# Revit family: LAMP_LUP DOWNLIGHT 110
name_source: partatom
category: Luminarias
revit_build: Autodesk Revit 2018 (Build: 20190510_1515(x64)
units: mm (PartAtom-declared; Revit-internal decimal feet)

## family parameters
Anfitrión = Cara
Compartido = No
Corte con vacíos al cargar = No
Cota de conector redondo = Diámetro de uso
Origen de luz = Sí
Punto de cálculo de habitación = No
Tipo de pieza = Normal

## types (8) — shared parameters
CRI = 80
Cambio de temperatura de color de luz atenuada = <Ninguno>
Diameter = 110 mm  [stored 0.360892 ft]
Elevación por defecto = 1219 mm
Filtro de color = 16777215
Finish = Texturised black RAL 9011
Gear = Electronic
Height = 155 mm  [stored 0.50853 ft]
Installation instructions = https://www.lamp.es
Insulation class = I
LED Lifetime = 50.000 L80 B10
Lamp = COB LED
Last update = 15/02/2022
MacAdam = 3
Manufacturer URL = http://www.lamp.es
Manufacturer country = Spain
Manufacturer name = LAMP
Material COB = LAMP_COB
Material cristal = LAMP_Cristal Bazz Transparente
Material cuerpo = LAMP_Aluminio Ocult Pendular NG
Material reflector = LAMP_Aluminio Reflector Imag
Product URL = https://www.lamp.es
Product datasheet = http://www.lamp.es
Protection rating = IP65 / IK06
Type = COB PHILIPS
Weight = 1.23 kg

## per-type parameters (varying)
| type | Archivo de red fotométrica | Efficacy | Plum | Power | Power Supply | Product code | Ángulo de inclinación |
| 600LM 3000 FLOOD BLACK | LS111005FL30NB.IES | 95 lm/W | 6 W | 5 W | 220-240V 50/60Hz | LS111005FL30NB | -90.00° |
| 624LM 3000 WIDE FLOOD BLACK | LS111005WF30NB.IES | 99 lm/W | 6 W | 5 W | 220-240V 50/60Hz | LS111005WF30NB | -90.00° |
| 626LM 4000 FLOOD BLACK | LS111005FL40NB.IES | 99 lm/W | 6 W | 5 W | 220-240V 50/60Hz | LS111005FL40NB | -90.00° |
| 650LM 4000 WIDE FLOOD BLACK | LS111005WF40NB.IES | 103 lm/W | 6 W | 5 W | 220-240V 50/60Hz | LS111005WF40NB | -90.00° |
| 963LM 3000 FLOOD BLACK | LS111010FL30NB.IES | 99 lm/W | 10 W | 8 W | 100-277V 50/60Hz | LS111010FL30NB | -90.00° |
| 1003LM 4000 FLOOD BLACK | LS111010FL40NB.IES | 103 lm/W | 10 W | 8 W | 100-277V 50/60Hz | LS111010FL40NB | 90.00° |
| 1008LM 3000 WIDE FLOOD BLACK | LS111010WF30NB.IES | 104 lm/W | 10 W | 8 W | 100-277V 50/60Hz | LS111010WF30NB | -90.00° |
| 1050LM 4000 WIDE FLOOD BLACK | LS111010WF40NB.IES | 108 lm/W | 10 W | 8 W | 100-277V 50/60Hz | LS111010WF40NB | -90.00° |

note: [stored X ft] marks values corroborated as IEEE doubles in the binary element streams (Revit-internal decimal feet)
